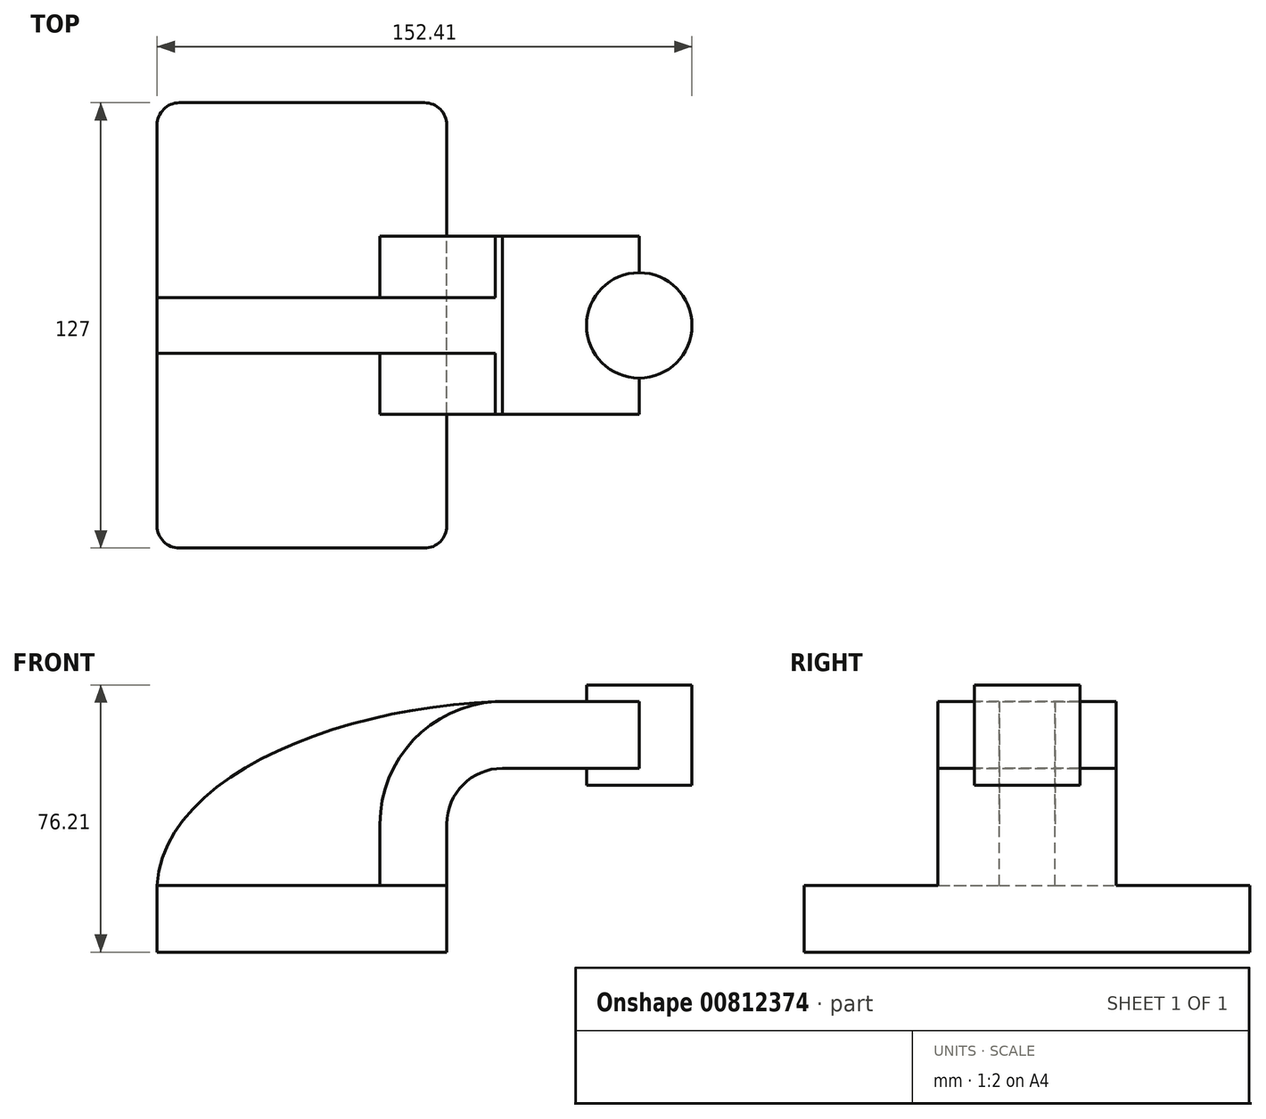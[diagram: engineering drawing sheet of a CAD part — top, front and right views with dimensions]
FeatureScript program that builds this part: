
annotation { "Feature Type Name" : "Feature", "Feature Type Description" : "" }
export const myFeature = defineFeature(function(context is Context, id is Id, definition is map)
    precondition{}
    {
        {
            var Q0;
            Q0=qCreatedBy(makeId("Front.planeOp"),FACE);
            var sketch = newSketch(context, id + "F0", { "sketchPlane" : qUnion([Q0])});
            skLineSegment(sketch, "E0.bottom", {"start": v(41.28, -9.52) * mm, "end": v(-41.28, -9.53) * mm});
            skLineSegment(sketch, "E0.top", {"start": v(41.28, 9.53) * mm, "end": v(-41.28, 9.53) * mm});
            skLineSegment(sketch, "E0.left", {"start": v(41.28, -9.52) * mm, "end": v(41.28, 9.53) * mm});
            skLineSegment(sketch, "E0.right", {"start": v(-41.28, -9.53) * mm, "end": v(-41.28, 9.53) * mm});
            skPoint(sketch, "E0.middle", {"position": v(0, 0) * mm});
            skLineSegment(sketch, "E1.bottom", {"start": v(111.12, 38.1) * mm, "end": v(60.32, 38.1) * mm});
            skLineSegment(sketch, "E1.top", {"start": v(111.12, 66.68) * mm, "end": v(60.32, 66.68) * mm});
            skLineSegment(sketch, "E1.left", {"start": v(111.12, 38.1) * mm, "end": v(111.12, 66.68) * mm});
            skLineSegment(sketch, "E1.right", {"start": v(60.32, 38.1) * mm, "end": v(60.33, 66.68) * mm});
            skPoint(sketch, "E1.middle", {"position": v(85.72, 52.39) * mm});
            skLineSegment(sketch, "E2", {"start": v(41.28, 9.53) * mm, "end": v(41.28, 27) * mm});
            skArc(sketch, "E3", {"start": v(41.27, 27) * mm, "mid": v(45.92, 38.23) * mm, "end": v(57.15, 42.88) * mm});
            skLineSegment(sketch, "E4", {"start": v(57.15, 42.88) * mm, "end": v(96.1, 42.88) * mm});
            skArc(sketch, "E5.0", {"start": v(22.23, 27) * mm, "mid": v(32.45, 51.7) * mm, "end": v(57.15, 61.93) * mm});
            skLineSegment(sketch, "E5.1", {"start": v(22.22, 9.53) * mm, "end": v(22.22, 27) * mm});
            skLineSegment(sketch, "E6.0", {"start": v(57.15, 61.93) * mm, "end": v(96.1, 61.93) * mm});
            skFitSpline(sketch, "E7", {"points": [v(-41.28, 9.53) * mm, v(57.15, 61.93) * mm], "startDerivative": vector(5.36, 94.38) * mm, "endDerivative": vector(136.58, 3.22) * mm});
            skLineSegment(sketch, "E8", {"start": v(96.1, 66.68) * mm, "end": v(96.1, 38.1) * mm});
            skSolve(sketch);
        }
        {
            var Q0;
            Q0=makeQuery(id+"F0.imprint","IMPRINT",FACE,{"disambiguationData":[TD([[makeQuery(id+"F0.imprint","IMPRINT",EDGE,{"derivedFrom":sQuery(id+"F0.wireOp",EDGE,"E0.bottom")}),-1.0]])]});
            extrude(context, id + "F1", {"entities" : qUnion([Q0]), "endBound" : BoundingType.SYMMETRIC, "depth" : 127 * mm, "offsetDistance" : 25.4 * mm});
        }
        {
            var Q0;
            {var subQ1=sQuery(id+"F0.wireOp",EDGE,"E2");Q0=makeQuery(id+"F0.imprint","IMPRINT",FACE,{"disambiguationData":[TD([[makeQuery(id+"F0.imprint","IMPRINT",EDGE,{"derivedFrom":subQ1}),1.0]])]});}
            var Q1;
            {var subQ0=sQuery(id+"F0.wireOp",EDGE,"E4");var subQ1=sQuery(id+"F0.wireOp",EDGE,"E1.right");var subQ2=makeQuery(id+"F0.imprint","INTERSECT",VERTEX,{"derivedFrom":[subQ1,subQ0]});Q1=makeQuery(id+"F0.imprint","IMPRINT",FACE,{"disambiguationData":[TD([[makeQuery(id+"F0.imprint","IMPRINT",EDGE,{"disambiguationData":[TD([[subQ2,-1.0]])],"derivedFrom":subQ1}),-1.0]])]});}
            extrude(context, id + "F2", {"entities" : qUnion([Q0, Q1]), "operationType" : NewBodyOperationType.ADD, "endBound" : BoundingType.SYMMETRIC, "depth" : 50.8 * mm, "offsetDistance" : 25.4 * mm});
        }
        {
            var Q0;
            {var subQ3=sQuery(id+"F0.wireOp",EDGE,"E5.1");Q0=makeQuery(id+"F0.imprint","IMPRINT",FACE,{"disambiguationData":[TD([[makeQuery(id+"F0.imprint","IMPRINT",EDGE,{"derivedFrom":subQ3}),1.0]])]});}
            extrude(context, id + "F3", {"entities" : qUnion([Q0]), "operationType" : NewBodyOperationType.ADD, "endBound" : BoundingType.SYMMETRIC, "depth" : 15.88 * mm, "offsetDistance" : 25.4 * mm});
        }
        {
            var Q0;
            {var subQ4=sQuery(id+"F0.wireOp",EDGE,"E1.left");Q0=makeQuery(id+"F0.imprint","IMPRINT",FACE,{"disambiguationData":[TD([[makeQuery(id+"F0.imprint","IMPRINT",EDGE,{"derivedFrom":subQ4}),1.0]])]});}
            var Q1;
            Q1=sQuery(id+"F0.wireOp",EDGE,"E8");
            revolve(context, id + "F4", {"operationType" : NewBodyOperationType.ADD, "surfaceOperationType" : NewSurfaceOperationType.NEW, "entities" : qUnion([Q0]), "axis" : qUnion([Q1]), "revolveType" : RevolveType.FULL});
        }
        {
            var Q0;
            Q0=makeQuery(id+"F1.opExtrude","CAP_EDGE",EDGE,{"disambiguationData":[OSD([sQuery(id+"F0.wireOp",EDGE,"E0.left")])],"isStart":false});
            var Q1;
            Q1=makeQuery(id+"F1.opExtrude","CAP_EDGE",EDGE,{"disambiguationData":[OSD([sQuery(id+"F0.wireOp",EDGE,"E0.right")])],"isStart":false});
            var Q2;
            Q2=makeQuery(id+"F1.opExtrude","CAP_EDGE",EDGE,{"disambiguationData":[OSD([sQuery(id+"F0.wireOp",EDGE,"E0.left")])],"isStart":true});
            var Q3;
            Q3=makeQuery(id+"F1.opExtrude","CAP_EDGE",EDGE,{"disambiguationData":[OSD([sQuery(id+"F0.wireOp",EDGE,"E0.right")])],"isStart":true});
            fillet(context, id + "F5", {"entities" : qUnion([Q0, Q1, Q2, Q3]), "radius" : 6.35 * mm, "tangentPropagation" : true, "allowEdgeOverflow" : false});
        }
    });
